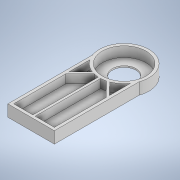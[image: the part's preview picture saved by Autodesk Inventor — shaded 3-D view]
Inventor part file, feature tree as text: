
AUTODESK INVENTOR PART (.ipt)
format: ipt  version: 2022 (Build 260153000, 153)  size: 168,960 bytes
history: native  units: mm
features: extrude x4, sketch x4, projected_geometry x1
ambient origin geometry x8: Origin, YZ Plane, XZ Plane, XY Plane, X Axis, Y Axis, Z Axis, Center Point
bodies: Solid1 (feature_tree)
feature tree (9):
  extrude  "Extrusion1"  Depth=160.0mm
  extrude  "Extrusion2"  Depth=150.0mm
  extrude  "Extrusion3"  Depth=5.0mm TaperAngle=0.0deg
  extrude  "Extrusion4"  Depth=10.0mm
  sketch  "Sketch1"  dims[d0=160.0mm d1=400.0mm]
  sketch  "Sketch2"  dims[d2=80.0mm d3=150.0mm]
  sketch  "Sketch3"  dims[d4=40.0mm d5=0.0mm d6=5.0mm d7=0.0mm]
  projected_geometry  "Projected Loop1"
  sketch  "Sketch4"  dims[d8=10.0mm d9=10.0mm d10=8.0mm d11=8.0mm d12=30.0mm d13=0.0mm d14=81.0mm d15=40.0mm d16=0.0mm]
